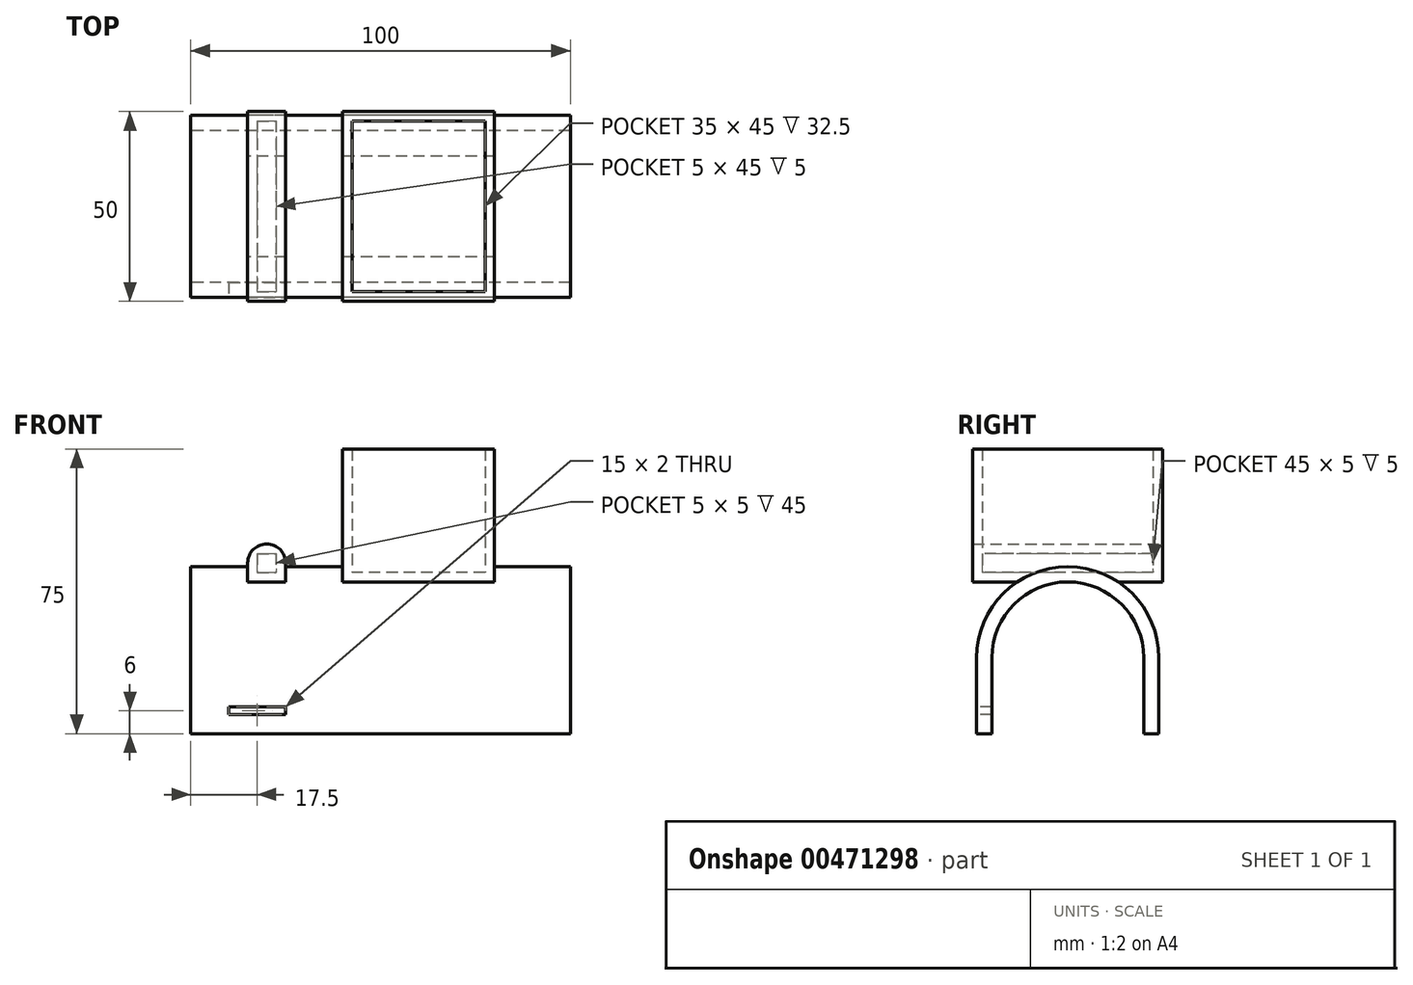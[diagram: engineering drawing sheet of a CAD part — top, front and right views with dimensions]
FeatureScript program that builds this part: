
annotation { "Feature Type Name" : "Feature", "Feature Type Description" : "" }
export const myFeature = defineFeature(function(context is Context, id is Id, definition is map)
    precondition{}
    {
        {
            var Q0;
            Q0=qCreatedBy(makeId("Right.planeOp"),FACE);
            var sketch = newSketch(context, id + "F0", { "sketchPlane" : qUnion([Q0])});
            skLineSegment(sketch, "E0.bottom", {"start": v(-20, 0) * mm, "end": v(-24, 0) * mm});
            skLineSegment(sketch, "E0.top", {"start": v(-20, 20) * mm, "end": v(-24, 20) * mm});
            skLineSegment(sketch, "E0.left", {"start": v(-20, 0) * mm, "end": v(-20, 20) * mm});
            skLineSegment(sketch, "E0.right", {"start": v(-24, 0) * mm, "end": v(-24, 20) * mm});
            skLineSegment(sketch, "E1.MirrorCS", {"start": v(20, 0) * mm, "end": v(24, 0) * mm});
            skLineSegment(sketch, "E2.MirrorCS", {"start": v(20, 20) * mm, "end": v(24, 20) * mm});
            skLineSegment(sketch, "E3.MirrorCS", {"start": v(24, 0) * mm, "end": v(24, 20) * mm});
            skLineSegment(sketch, "E4.MirrorCS", {"start": v(20, 0) * mm, "end": v(20, 20) * mm});
            skArc(sketch, "E5", {"start": v(20, 20) * mm, "mid": v(0, 40) * mm, "end": v(-20, 20) * mm});
            skArc(sketch, "E6", {"start": v(24, 20) * mm, "mid": v(0, 44) * mm, "end": v(-24, 20) * mm});
            skSolve(sketch);
        }
        {
            var Q0;
            Q0=qCreatedBy(makeId("Top.planeOp"),FACE);
            cPlane(context, id + "F1", {"entities" : qUnion([Q0]), "cplaneType" : CPlaneType.OFFSET, "offset" : 40 * mm, "width" : 150 * mm, "height" : 150 * mm});
        }
        {
            var Q0;
            Q0=qSketchRegion(id+"F0",true);
            extrude(context, id + "F2", {"entities" : qUnion([Q0]), "depth" : 100 * mm});
        }
        {
            var Q0;
            Q0=qCreatedBy(id+"F1.planeOp",FACE);
            var sketch = newSketch(context, id + "F3", { "sketchPlane" : qUnion([Q0])});
            skLineSegment(sketch, "E7.bottom", {"start": v(15, 25) * mm, "end": v(25, 25) * mm});
            skLineSegment(sketch, "E7.top", {"start": v(15, -25) * mm, "end": v(25, -25) * mm});
            skLineSegment(sketch, "E7.left", {"start": v(15, 25) * mm, "end": v(15, -25) * mm});
            skLineSegment(sketch, "E7.right", {"start": v(25, 25) * mm, "end": v(25, -25) * mm});
            skLineSegment(sketch, "E8.bottom", {"start": v(80, 25) * mm, "end": v(40, 25) * mm});
            skLineSegment(sketch, "E8.top", {"start": v(80, -25) * mm, "end": v(40, -25) * mm});
            skLineSegment(sketch, "E8.left", {"start": v(80, 25) * mm, "end": v(80, -25) * mm});
            skLineSegment(sketch, "E8.right", {"start": v(40, 25) * mm, "end": v(40, -25) * mm});
            skSolve(sketch);
        }
        {
            var Q0;
            Q0=qSketchRegion(id+"F3",true);
            extrude(context, id + "F4", {"entities" : qUnion([Q0]), "operationType" : NewBodyOperationType.ADD, "depth" : 10 * mm});
        }
        {
            var Q0;
            Q0=makeQuery(id+"F4.opExtrude","CAP_FACE",FACE,{"disambiguationData":[OSD([sQuery(id+"F3.wireOp",EDGE,"E8.bottom"),sQuery(id+"F3.wireOp",EDGE,"E8.top"),sQuery(id+"F3.wireOp",EDGE,"E8.left"),sQuery(id+"F3.wireOp",EDGE,"E8.right")])],"isStart":false});
            extrude(context, id + "F5", {"entities" : qUnion([Q0]), "operationType" : NewBodyOperationType.ADD, "depth" : 25 * mm});
        }
        {
            var Q0;
            Q0=makeQuery(id+"F5.opExtrude","CAP_FACE",FACE,{"disambiguationData":[OSD([sQuery(id+"F3.wireOp",EDGE,"E8.bottom"),sQuery(id+"F3.wireOp",EDGE,"E8.top"),sQuery(id+"F3.wireOp",EDGE,"E8.left"),sQuery(id+"F3.wireOp",EDGE,"E8.right")])],"isStart":false});
            shell(context, id + "F6", {"entities" : qUnion([Q0]), "thickness" : 2.5 * mm});
        }
        {
            var Q0;
            Q0=makeQuery(id+"F4.opExtrude","CAP_EDGE",EDGE,{"disambiguationData":[OSD([sQuery(id+"F3.wireOp",EDGE,"E7.left")])],"isStart":false});
            fillet(context, id + "F7", {"entities" : qUnion([Q0]), "radius" : 5 * mm, "tangentPropagation" : true, "allowEdgeOverflow" : false});
        }
        {
            var Q0;
            Q0=makeQuery(id+"F4.opExtrude","CAP_EDGE",EDGE,{"disambiguationData":[OSD([sQuery(id+"F3.wireOp",EDGE,"E7.right")])],"isStart":false});
            fillet(context, id + "F8", {"entities" : qUnion([Q0]), "radius" : 5 * mm, "tangentPropagation" : true, "allowEdgeOverflow" : false});
        }
        {
            var Q0;
            Q0=makeQuery(id+"F2.opExtrude","SWEPT_FACE",FACE,{"disambiguationData":[OSD([sQuery(id+"F0.wireOp",EDGE,"E0.right")])]});
            var sketch = newSketch(context, id + "F9", { "sketchPlane" : qUnion([Q0])});
            skLineSegment(sketch, "E9.bottom", {"start": v(10, 7) * mm, "end": v(25, 7) * mm});
            skLineSegment(sketch, "E9.top", {"start": v(10, 5) * mm, "end": v(25, 5) * mm});
            skLineSegment(sketch, "E9.left", {"start": v(10, 7) * mm, "end": v(10, 5) * mm});
            skLineSegment(sketch, "E9.right", {"start": v(25, 7) * mm, "end": v(25, 5) * mm});
            skSolve(sketch);
        }
        {
            var Q0;
            Q0=makeQuery(id+"F9.imprint","IMPRINT",FACE,{"disambiguationData":[TD([[makeQuery(id+"F9.imprint","IMPRINT",EDGE,{"derivedFrom":sQuery(id+"F9.wireOp",EDGE,"E9.bottom")}),-1.0]])]});
            extrude(context, id + "F10", {"entities" : qUnion([Q0]), "operationType" : NewBodyOperationType.REMOVE, "oppositeDirection" : true, "depth" : 25 * mm});
        }
    });
